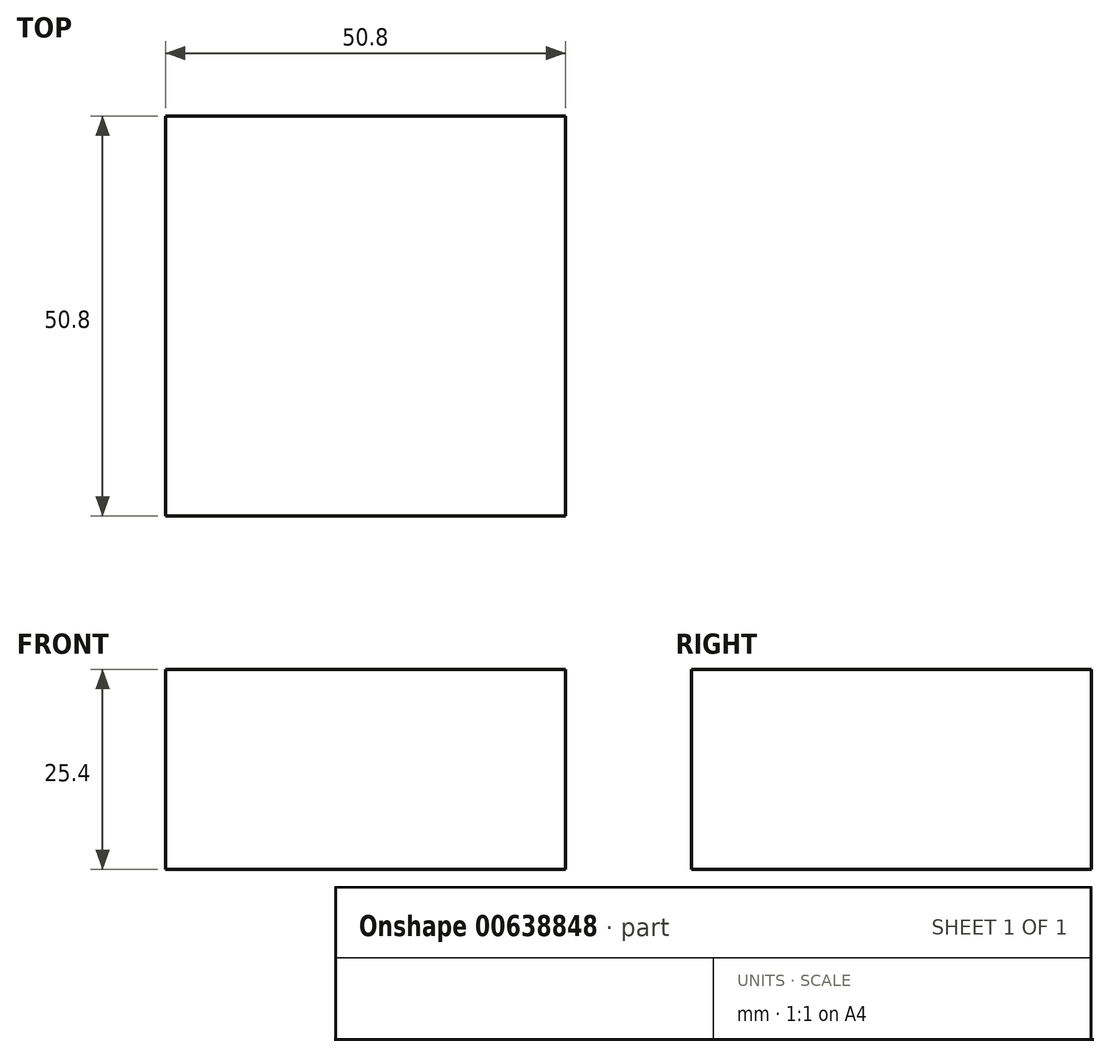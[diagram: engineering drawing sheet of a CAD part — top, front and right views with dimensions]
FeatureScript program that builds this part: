
annotation { "Feature Type Name" : "Feature", "Feature Type Description" : "" }
export const myFeature = defineFeature(function(context is Context, id is Id, definition is map)
    precondition{}
    {
        {
            var Q0;
            Q0=qCreatedBy(makeId("Top.planeOp"),FACE);
            var sketch = newSketch(context, id + "F0", { "sketchPlane" : qUnion([Q0])});
            skLineSegment(sketch, "E0.bottom", {"start": v(-25.4, 25.4) * mm, "end": v(25.4, 25.4) * mm});
            skLineSegment(sketch, "E0.top", {"start": v(-25.4, -25.4) * mm, "end": v(25.4, -25.4) * mm});
            skLineSegment(sketch, "E0.left", {"start": v(-25.4, 25.4) * mm, "end": v(-25.4, -25.4) * mm});
            skLineSegment(sketch, "E0.right", {"start": v(25.4, 25.4) * mm, "end": v(25.4, -25.4) * mm});
            skPoint(sketch, "E0.middle", {"position": v(0, 0) * mm});
            skSolve(sketch);
        }
        {
            var Q0;
            Q0 = qSketchRegion(id + "F0", true);
            extrude(context, id + "F1", {"entities" : qUnion([Q0]), "depth" : 25.4 * mm, "offsetDistance" : 25.4 * mm});
        }
    });
